# Revit family: SANINDUSA_134025004_Look_LookFDRimFlushCloseCoupledToilet345x648x398_V0
name_source: partatom
category: Plumbing Fixtures
units: mm (PartAtom-declared; Revit-internal decimal feet)

## family parameters
Cut with Voids When Loaded = No
Host = Face
Part Type = Normal
Room Calculation Point = No
Round Connector Dimension = Use Diameter
Shared = No

## types (1)
- SANINDUSA_134025004_Look_LookFDRimFlushCloseCoupledToilet345x648x398_V0
    AssetType = Fixed
    CodePerformance = EN 997:2012+A1:2015    CL 1 - 6 A
    Color = white
    Constituents = Compatible toilet seats (not included): 2341100-Look toilet seat with clipoff system; 2343100-Look toilet seat with clipoff and slowclose system.
    Default Elevation = 1219 mm
    Description = Soil appliance for the disposal of excrement.
    DrainSize = 90 mm  [stored 0.295276 ft]
    Element Type = TOILETPAN: Soil appliance for the disposal of excrement.
    Features = Domestic and commercial use. With rimflush discharge system without rim, which promotes hygiene,
make easier the toilet cleaning and reduces the proliferation of germs. Toilet seat with clipoff system easy to clean and slow close.
    Finish = gloss
    InletDiameter = 0 mm  [stored 0 ft]
    Installation Instructions = https://www.tec.sanindusa.pt
    Manufacturer = Sanindusa
    ManufacturerName = Sanindusa
    ManufacturerURL = www.tec.sanindusa.pt
    Material = vitreous china
    Model = 134025004
    ModelNumber = 134025004
    ModelReference = Look
    Name = Look rimflush close coupled toilet
    NominalHeight = 398 mm  [stored 1.30577 ft]
    NominalLength = 345 mm  [stored 1.13189 ft]
    NominalWidth = 648 mm  [stored 2.12598 ft]
    PanColor = white
    PanMaterial = vitreous china
    PanMounting = pedestal
    Pre-defined type (IFC) = TOILETPAN
    ProductInformation = https://www.tec.sanindusa.pt
    ProductionYear = 2021
    Size = 345x648x398
    ToiletPanType = washdown
    ToiletType = LooseCoupled
    URL = www.tec.sanindusa.pt
    Version = 1
    WarrantyDescription = https://www.tec.sanindusa.pt
    WarrantyDurationParts = 5
    WarrantyDurationUnit = year
    Waste Connection = Yes
    Weight = 32.90 kg

note: [stored X ft] marks values corroborated as IEEE doubles in the binary element streams (Revit-internal decimal feet)

## geometry (parser evidence)
native form markers: Sweep x7
no freeform markers — native parametric forms only
